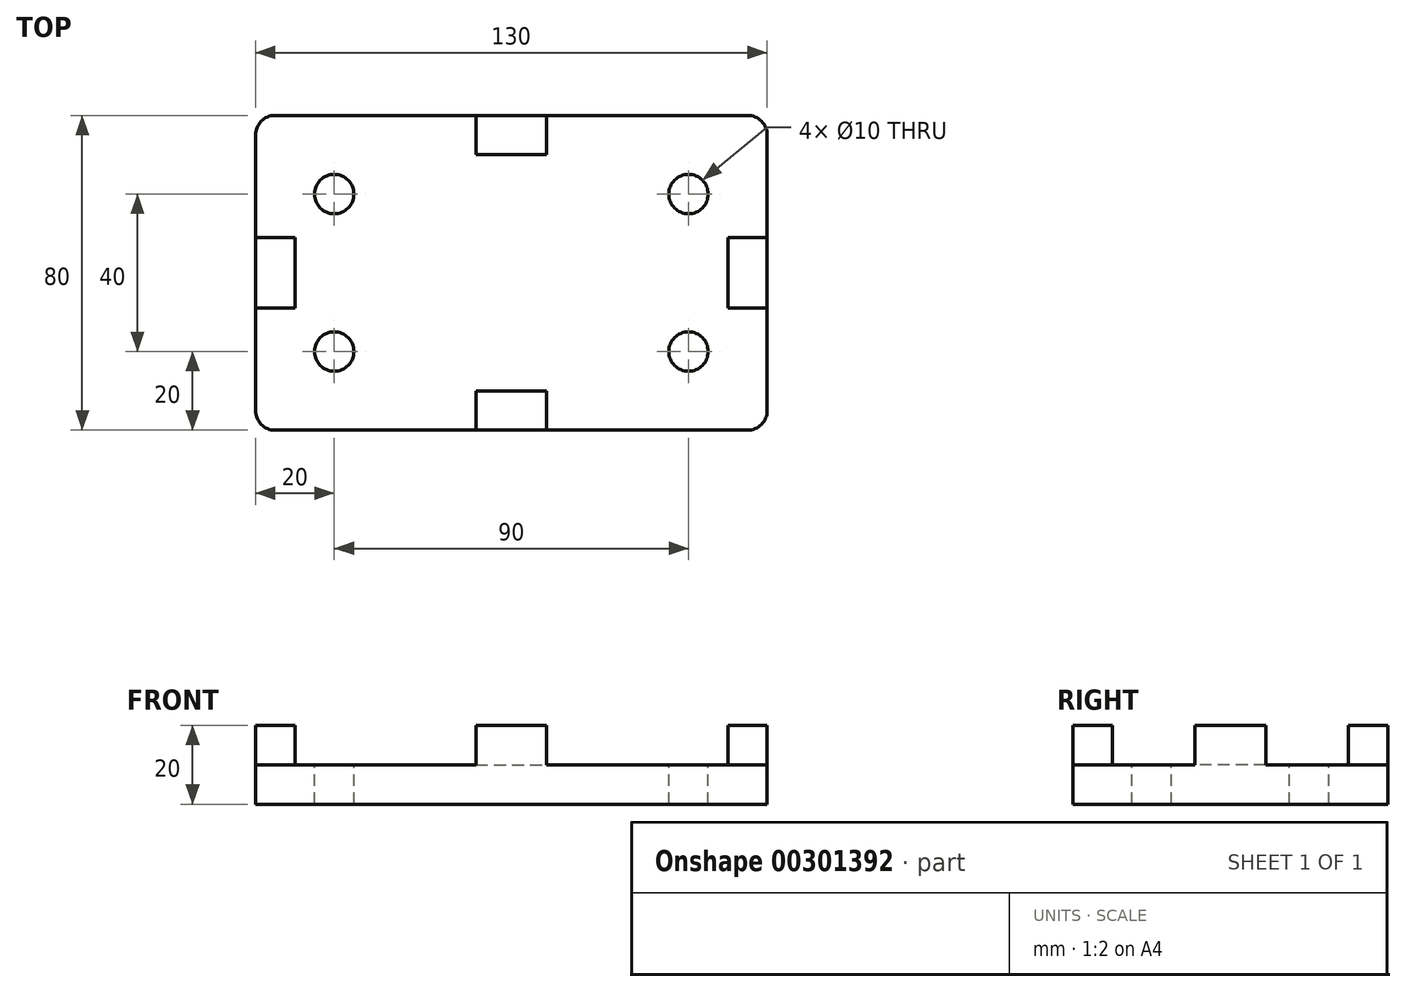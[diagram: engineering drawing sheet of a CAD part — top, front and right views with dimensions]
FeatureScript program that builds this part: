
annotation { "Feature Type Name" : "Feature", "Feature Type Description" : "" }
export const myFeature = defineFeature(function(context is Context, id is Id, definition is map)
    precondition{}
    {
        {
            var Q0;
            Q0=qCreatedBy(makeId("Top.planeOp"),FACE);
            var sketch = newSketch(context, id + "F0", { "sketchPlane" : qUnion([Q0])});
            skLineSegment(sketch, "E0", {"start": v(0, 40) * mm, "end": v(-65, 40) * mm});
            skLineSegment(sketch, "E1.MirrorCS", {"start": v(0, 40) * mm, "end": v(65, 40) * mm});
            skLineSegment(sketch, "E2.MirrorCS", {"start": v(0, -40) * mm, "end": v(-65, -40) * mm});
            skLineSegment(sketch, "E3.MirrorCS", {"start": v(0, -40) * mm, "end": v(65, -40) * mm});
            skLineSegment(sketch, "E4", {"start": v(-65, 40) * mm, "end": v(-65, -40) * mm});
            skLineSegment(sketch, "E5", {"start": v(65, -40) * mm, "end": v(65, 40) * mm});
            skSolve(sketch);
        }
        {
            var Q0;
            Q0 = qSketchRegion(id + "F0", true);
            extrude(context, id + "F1", {"entities" : qUnion([Q0]), "depth" : 10 * mm});
        }
        {
            var Q0;
            Q0=makeQuery(id+"F1.opExtrude","CAP_FACE",FACE,{"disambiguationData":[OSD([sQuery(id+"F0.wireOp",EDGE,"E0"),sQuery(id+"F0.wireOp",EDGE,"E1.MirrorCS"),sQuery(id+"F0.wireOp",EDGE,"E2.MirrorCS"),sQuery(id+"F0.wireOp",EDGE,"E3.MirrorCS"),sQuery(id+"F0.wireOp",EDGE,"E4"),sQuery(id+"F0.wireOp",EDGE,"E5")])],"isStart":false});
            var sketch = newSketch(context, id + "F2", { "sketchPlane" : qUnion([Q0])});
            skLineSegment(sketch, "E6", {"start": v(0, 30) * mm, "end": v(9, 30) * mm});
            skLineSegment(sketch, "E7", {"start": v(9, 30) * mm, "end": v(9, 40) * mm});
            skLineSegment(sketch, "E8", {"start": v(9, 40) * mm, "end": v(-9, 40) * mm});
            skLineSegment(sketch, "E9", {"start": v(-9, 40) * mm, "end": v(-9, 30) * mm});
            skLineSegment(sketch, "E10", {"start": v(-9, 30) * mm, "end": v(0, 30) * mm});
            skLineSegment(sketch, "E11.MirrorCS", {"start": v(0, -30) * mm, "end": v(9, -30) * mm});
            skLineSegment(sketch, "E12.MirrorCS", {"start": v(-9, -30) * mm, "end": v(0, -30) * mm});
            skLineSegment(sketch, "E13.MirrorCS", {"start": v(-9, -40) * mm, "end": v(-9, -30) * mm});
            skLineSegment(sketch, "E14.MirrorCS", {"start": v(9, -30) * mm, "end": v(9, -40) * mm});
            skLineSegment(sketch, "E15", {"start": v(-65, 0) * mm, "end": v(-65, 9) * mm});
            skLineSegment(sketch, "E16", {"start": v(-65, 9) * mm, "end": v(-55, 9) * mm});
            skLineSegment(sketch, "E17", {"start": v(-55, 9) * mm, "end": v(-55, -9) * mm});
            skLineSegment(sketch, "E18", {"start": v(-55, -9) * mm, "end": v(-65, -9) * mm});
            skLineSegment(sketch, "E19", {"start": v(-65, -9) * mm, "end": v(-65, 0) * mm});
            skLineSegment(sketch, "E20.MirrorCS", {"start": v(55, 9) * mm, "end": v(55, -9) * mm});
            skLineSegment(sketch, "E21.MirrorCS", {"start": v(65, 9) * mm, "end": v(55, 9) * mm});
            skLineSegment(sketch, "E22.MirrorCS", {"start": v(55, -9) * mm, "end": v(65, -9) * mm});
            skLineSegment(sketch, "E23.0.0", {"start": v(-65, -40) * mm, "end": v(65, -40) * mm});
            skLineSegment(sketch, "E23.0.1", {"start": v(65, -40) * mm, "end": v(65, 40) * mm});
            skLineSegment(sketch, "E23.0.2", {"start": v(65, 40) * mm, "end": v(-65, 40) * mm});
            skLineSegment(sketch, "E23.0.3", {"start": v(-65, 40) * mm, "end": v(-65, -40) * mm});
            skSolve(sketch);
        }
        {
            var Q0;
            Q0=makeQuery(id+"F2.imprint","IMPRINT",FACE,{"disambiguationData":[TD([[makeQuery(id+"F2.imprint","IMPRINT",EDGE,{"derivedFrom":sQuery(id+"F2.wireOp",EDGE,"E6")}),1.0]])]});
            var Q1;
            Q1=makeQuery(id+"F2.imprint","IMPRINT",FACE,{"disambiguationData":[TD([[makeQuery(id+"F2.imprint","IMPRINT",EDGE,{"derivedFrom":sQuery(id+"F2.wireOp",EDGE,"E20.MirrorCS")}),1.0]])]});
            var Q2;
            {var subQ0=sQuery(id+"F2.wireOp",EDGE,"E16");Q2=makeQuery(id+"F2.imprint","IMPRINT",FACE,{"disambiguationData":[TD([[makeQuery(id+"F2.imprint","IMPRINT",EDGE,{"derivedFrom":subQ0}),-1.0]])]});}
            var Q3;
            Q3=makeQuery(id+"F2.imprint","IMPRINT",FACE,{"disambiguationData":[TD([[makeQuery(id+"F2.imprint","IMPRINT",EDGE,{"derivedFrom":sQuery(id+"F2.wireOp",EDGE,"E11.MirrorCS")}),-1.0]])]});
            extrude(context, id + "F3", {"entities" : qUnion([Q0, Q1, Q2, Q3]), "operationType" : NewBodyOperationType.ADD, "depth" : 10 * mm});
        }
        {
            var Q0;
            Q0=makeQuery(id+"F1.opExtrude","CAP_FACE",FACE,{"disambiguationData":[OSD([sQuery(id+"F0.wireOp",EDGE,"E0"),sQuery(id+"F0.wireOp",EDGE,"E1.MirrorCS"),sQuery(id+"F0.wireOp",EDGE,"E2.MirrorCS"),sQuery(id+"F0.wireOp",EDGE,"E3.MirrorCS"),sQuery(id+"F0.wireOp",EDGE,"E4"),sQuery(id+"F0.wireOp",EDGE,"E5")])],"isStart":false});
            var sketch = newSketch(context, id + "F4", { "sketchPlane" : qUnion([Q0])});
            skLineSegment(sketch, "E24", {"start": v(65, -40) * mm, "end": v(45, -40) * mm});
            skLineSegment(sketch, "E25", {"start": v(65, -40) * mm, "end": v(65, -20) * mm});
            skLineSegment(sketch, "E26", {"start": v(-65, -40) * mm, "end": v(-65, -20) * mm});
            skCircle(sketch, "E27", {"center": v(-45, -20) * mm, "radius": 5 * mm});
            skCircle(sketch, "E28", {"center": v(45, -20) * mm, "radius": 5 * mm});
            skCircle(sketch, "E29", {"center": v(45, 20) * mm, "radius": 5 * mm});
            skCircle(sketch, "E30", {"center": v(-45, 20) * mm, "radius": 5 * mm});
            skSolve(sketch);
        }
        {
            var Q0;
            Q0 = qSketchRegion(id + "F4", true);
            extrude(context, id + "F5", {"entities" : qUnion([Q0]), "operationType" : NewBodyOperationType.REMOVE, "endBound" : BoundingType.THROUGH_ALL, "oppositeDirection" : true, "depth" : 25 * mm});
        }
        {
            var Q0;
            Q0 = qSketchRegion(id + "F4", true);
            extrude(context, id + "F6", {"entities" : qUnion([Q0]), "operationType" : NewBodyOperationType.REMOVE, "endBound" : BoundingType.THROUGH_ALL, "oppositeDirection" : true, "depth" : 25 * mm});
        }
        {
            var Q0;
            Q0=makeQuery(id+"F1.opExtrude","SWEPT_EDGE",EDGE,{"disambiguationData":[OSD([sQuery(id+"F0.wireOp",EDGE,"E2.MirrorCS"),sQuery(id+"F0.wireOp",EDGE,"E4")])]});
            var Q1;
            Q1=makeQuery(id+"F1.opExtrude","SWEPT_EDGE",EDGE,{"disambiguationData":[OSD([sQuery(id+"F0.wireOp",EDGE,"E3.MirrorCS"),sQuery(id+"F0.wireOp",EDGE,"E5")])]});
            var Q2;
            Q2=makeQuery(id+"F1.opExtrude","SWEPT_EDGE",EDGE,{"disambiguationData":[OSD([sQuery(id+"F0.wireOp",EDGE,"E1.MirrorCS"),sQuery(id+"F0.wireOp",EDGE,"E5")])]});
            var Q3;
            Q3=makeQuery(id+"F1.opExtrude","SWEPT_EDGE",EDGE,{"disambiguationData":[OSD([sQuery(id+"F0.wireOp",EDGE,"E0"),sQuery(id+"F0.wireOp",EDGE,"E4")])]});
            fillet(context, id + "F7", {"entities" : qUnion([Q0, Q1, Q2, Q3]), "radius" : 5 * mm, "tangentPropagation" : true, "allowEdgeOverflow" : false});
        }
    });
